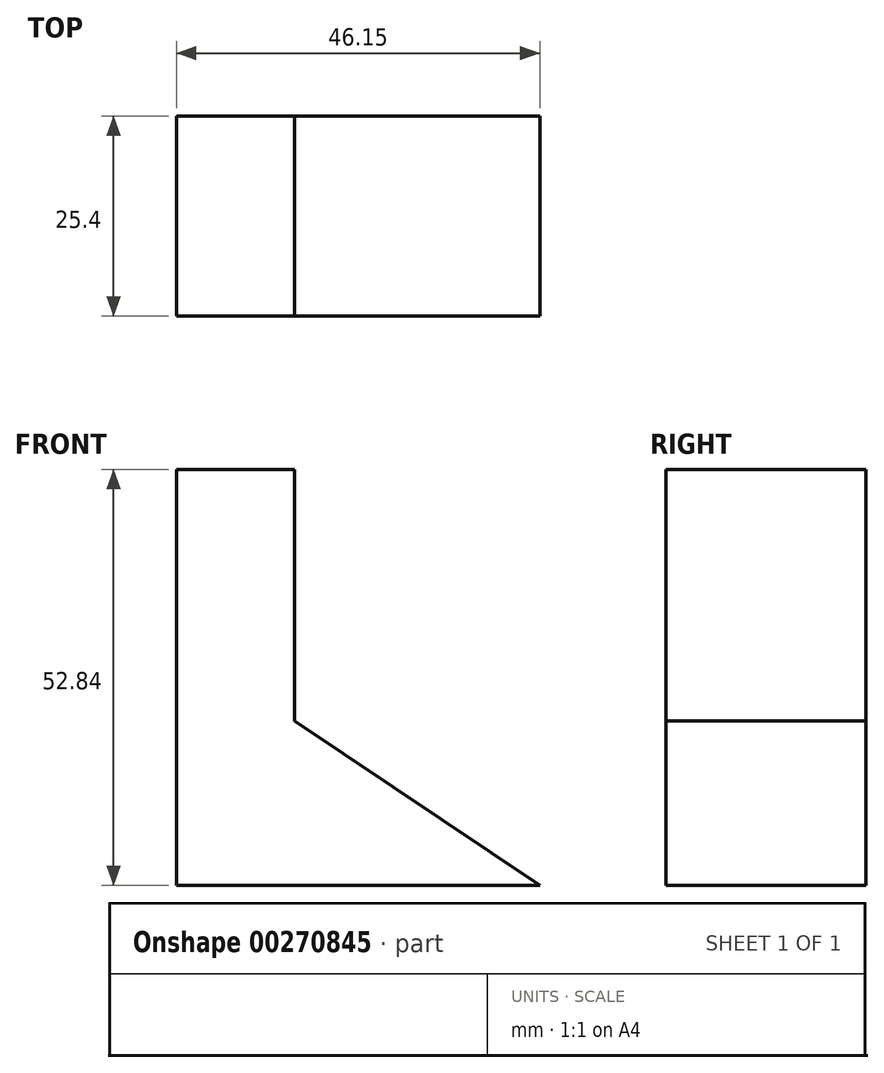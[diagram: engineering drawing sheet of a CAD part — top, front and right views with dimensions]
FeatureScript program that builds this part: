
annotation { "Feature Type Name" : "Feature", "Feature Type Description" : "" }
export const myFeature = defineFeature(function(context is Context, id is Id, definition is map)
    precondition{}
    {
        {
            var Q0;
            Q0=qCreatedBy(makeId("Front.planeOp"),FACE);
            var sketch = newSketch(context, id + "F0", { "sketchPlane" : qUnion([Q0])});
            skLineSegment(sketch, "E0", {"start": v(0, 0) * mm, "end": v(-46.15, 0) * mm});
            skLineSegment(sketch, "E1", {"start": v(-46.15, 0) * mm, "end": v(-46.15, 52.84) * mm});
            skLineSegment(sketch, "E2", {"start": v(-46.15, 52.84) * mm, "end": v(-31.16, 52.84) * mm});
            skLineSegment(sketch, "E3", {"start": v(-31.16, 52.84) * mm, "end": v(-31.16, 20.88) * mm});
            skLineSegment(sketch, "E4", {"start": v(-31.16, 20.88) * mm, "end": v(0, 0) * mm});
            skSolve(sketch);
        }
        {
            var Q0;
            Q0 = qSketchRegion(id + "F0", true);
            extrude(context, id + "F1", {"entities" : qUnion([Q0]), "depth" : 25.4 * mm});
        }
    });
